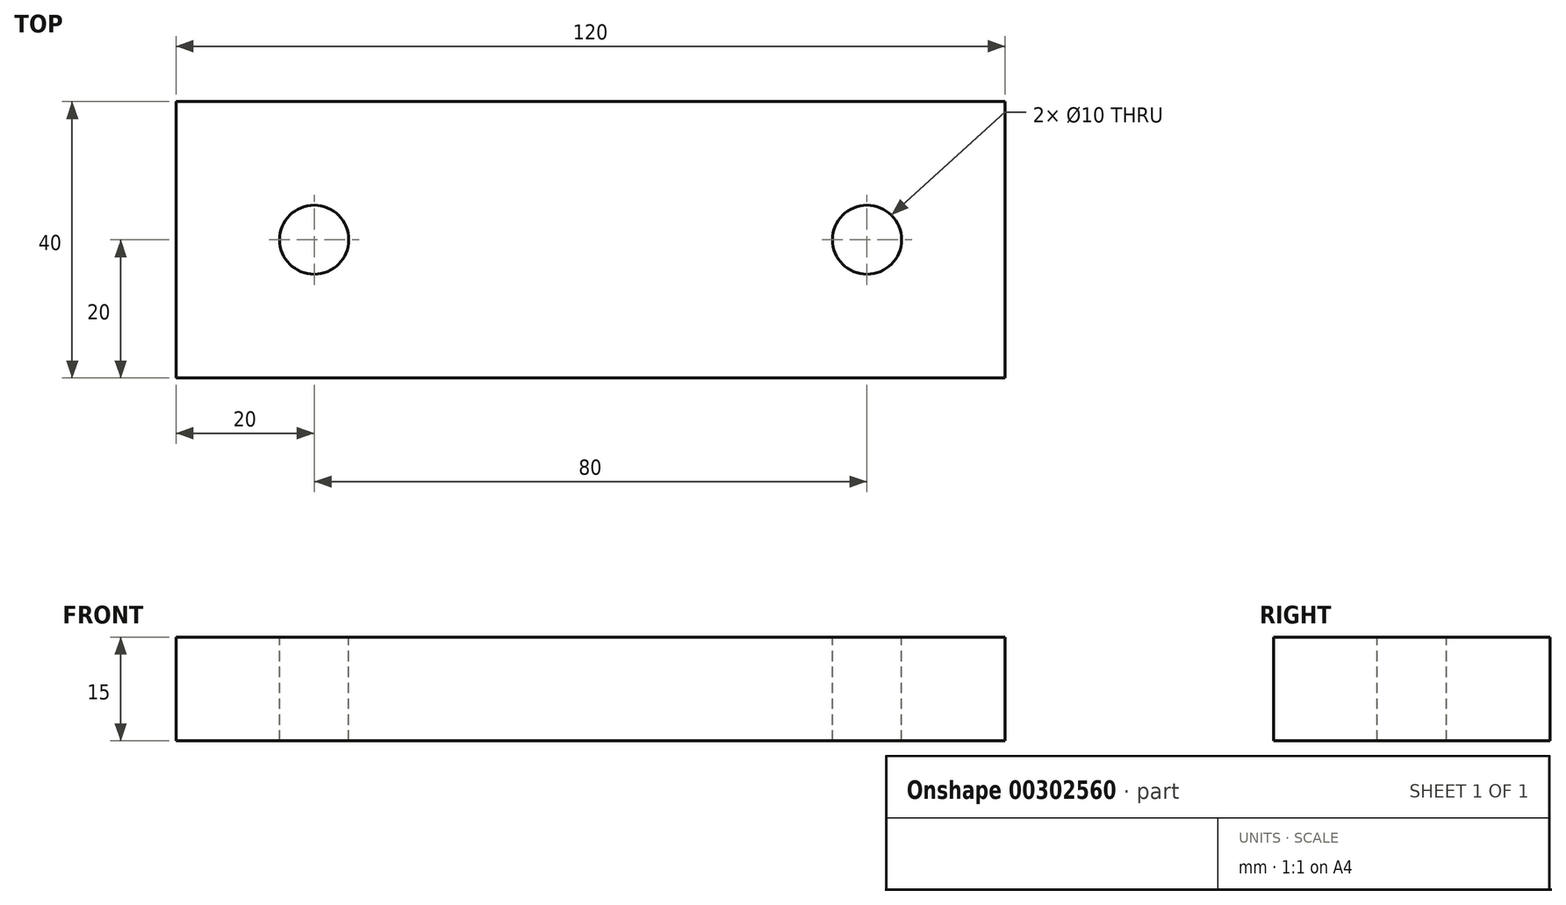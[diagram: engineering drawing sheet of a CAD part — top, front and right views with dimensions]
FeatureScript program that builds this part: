
annotation { "Feature Type Name" : "Feature", "Feature Type Description" : "" }
export const myFeature = defineFeature(function(context is Context, id is Id, definition is map)
    precondition{}
    {
        {
            var Q0;
            Q0=qCreatedBy(makeId("Front.planeOp"),FACE);
            var sketch = newSketch(context, id + "F0", { "sketchPlane" : qUnion([Q0])});
            skLineSegment(sketch, "E0.bottom", {"start": v(0, 0) * mm, "end": v(120, 0) * mm});
            skLineSegment(sketch, "E0.top", {"start": v(0, 15) * mm, "end": v(120, 15) * mm});
            skLineSegment(sketch, "E0.left", {"start": v(0, 0) * mm, "end": v(0, 15) * mm});
            skLineSegment(sketch, "E0.right", {"start": v(120, 0) * mm, "end": v(120, 15) * mm});
            skSolve(sketch);
        }
        {
            var Q0;
            Q0 = qSketchRegion(id + "F0", true);
            extrude(context, id + "F1", {"entities" : qUnion([Q0]), "endBound" : BoundingType.SYMMETRIC, "depth" : 40 * mm});
        }
        {
            var Q0;
            Q0=makeQuery(id+"F1.opExtrude","SWEPT_FACE",FACE,{"disambiguationData":[OSD([sQuery(id+"F0.wireOp",EDGE,"E0.top")])]});
            var sketch = newSketch(context, id + "F2", { "sketchPlane" : qUnion([Q0])});
            skCircle(sketch, "E1", {"center": v(20, 0) * mm, "radius": 5 * mm});
            skCircle(sketch, "E2", {"center": v(100, 0) * mm, "radius": 5 * mm});
            skSolve(sketch);
        }
        {
            var Q0;
            Q0 = qSketchRegion(id + "F2", true);
            extrude(context, id + "F3", {"entities" : qUnion([Q0]), "operationType" : NewBodyOperationType.REMOVE, "oppositeDirection" : true, "depth" : 25 * mm});
        }
    });
